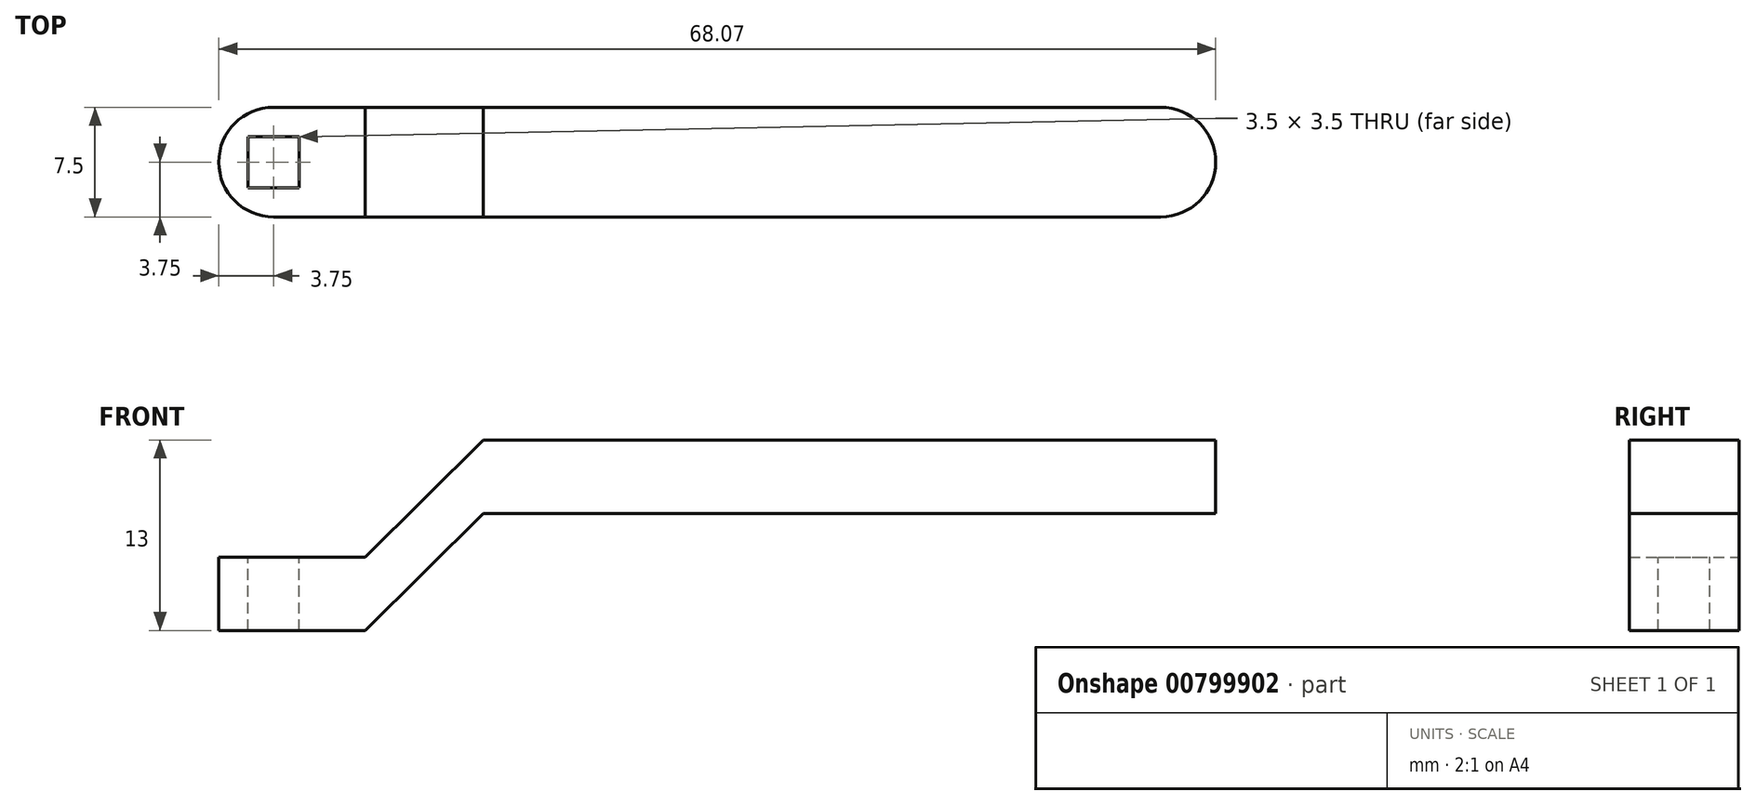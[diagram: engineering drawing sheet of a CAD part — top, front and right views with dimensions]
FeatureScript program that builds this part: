
annotation { "Feature Type Name" : "Feature", "Feature Type Description" : "" }
export const myFeature = defineFeature(function(context is Context, id is Id, definition is map)
    precondition{}
    {
        {
            var Q0;
            Q0=qCreatedBy(makeId("Front.planeOp"),FACE);
            var sketch = newSketch(context, id + "F0", { "sketchPlane" : qUnion([Q0])});
            skLineSegment(sketch, "E0", {"start": v(0, 0) * mm, "end": v(10, 0) * mm});
            skLineSegment(sketch, "E1", {"start": v(10, 0) * mm, "end": v(18.07, 8) * mm});
            skLineSegment(sketch, "E2", {"start": v(18.07, 8) * mm, "end": v(68.07, 8) * mm});
            skLineSegment(sketch, "E3", {"start": v(68.07, 8) * mm, "end": v(68.07, 13) * mm});
            skLineSegment(sketch, "E4", {"start": v(68.07, 13) * mm, "end": v(18.07, 13) * mm});
            skLineSegment(sketch, "E5", {"start": v(18.07, 13) * mm, "end": v(10, 5) * mm});
            skLineSegment(sketch, "E6", {"start": v(10, 5) * mm, "end": v(0, 5) * mm});
            skLineSegment(sketch, "E7", {"start": v(0, 5) * mm, "end": v(0, 0) * mm});
            skSolve(sketch);
        }
        {
            var Q0;
            Q0=makeQuery(id+"F0.imprint","IMPRINT",FACE,{"disambiguationData":[TD([[makeQuery(id+"F0.imprint","IMPRINT",EDGE,{"derivedFrom":sQuery(id+"F0.wireOp",EDGE,"E0")}),1.0]])]});
            extrude(context, id + "F1", {"entities" : qUnion([Q0]), "depth" : 3.75 * mm, "offsetDistance" : 25.4 * mm, "hasSecondDirection" : true, "secondDirectionOppositeDirection" : true, "secondDirectionDepth" : 3.75 * mm});
        }
        {
            var Q0;
            Q0=makeQuery(id+"F1.opExtrude","SWEPT_FACE",FACE,{"disambiguationData":[OSD([sQuery(id+"F0.wireOp",EDGE,"E6")])]});
            var sketch = newSketch(context, id + "F2", { "sketchPlane" : qUnion([Q0])});
            skPoint(sketch, "E8.centerSnap0", {"position": v(3.75, -3.75) * mm});
            skLineSegment(sketch, "E9.bottom", {"start": v(2, -1.75) * mm, "end": v(5.5, -1.75) * mm});
            skLineSegment(sketch, "E9.top", {"start": v(2, 1.75) * mm, "end": v(5.5, 1.75) * mm});
            skLineSegment(sketch, "E9.left", {"start": v(2, -1.75) * mm, "end": v(2, 1.75) * mm});
            skLineSegment(sketch, "E9.right", {"start": v(5.5, -1.75) * mm, "end": v(5.5, 1.75) * mm});
            skPoint(sketch, "E9.middle", {"position": v(3.75, 0) * mm});
            skSolve(sketch);
        }
        {
            var Q0;
            Q0=makeQuery(id+"F2.imprint","IMPRINT",FACE,{"disambiguationData":[TD([[makeQuery(id+"F2.imprint","IMPRINT",EDGE,{"derivedFrom":sQuery(id+"F2.wireOp",EDGE,"E9.bottom")}),1.0]])]});
            extrude(context, id + "F3", {"entities" : qUnion([Q0]), "operationType" : NewBodyOperationType.REMOVE, "endBound" : BoundingType.THROUGH_ALL, "oppositeDirection" : true, "depth" : 5 * mm, "offsetDistance" : 25.4 * mm});
        }
        {
            var Q0;
            Q0=makeQuery(id+"F1.opExtrude","CAP_EDGE",EDGE,{"disambiguationData":[OSD([sQuery(id+"F0.wireOp",EDGE,"E7")])],"isStart":false});
            var Q1;
            Q1=makeQuery(id+"F1.opExtrude","CAP_EDGE",EDGE,{"disambiguationData":[OSD([sQuery(id+"F0.wireOp",EDGE,"E7")])],"isStart":true});
            fillet(context, id + "F4", {"entities" : qUnion([Q0, Q1]), "radius" : 3.75 * mm, "tangentPropagation" : true, "allowEdgeOverflow" : false});
        }
        {
            var Q0;
            Q0=makeQuery(id+"F1.opExtrude","CAP_EDGE",EDGE,{"disambiguationData":[OSD([sQuery(id+"F0.wireOp",EDGE,"E3")])],"isStart":false});
            var Q1;
            Q1=makeQuery(id+"F1.opExtrude","CAP_EDGE",EDGE,{"disambiguationData":[OSD([sQuery(id+"F0.wireOp",EDGE,"E3")])],"isStart":true});
            fillet(context, id + "F5", {"entities" : qUnion([Q0, Q1]), "radius" : 3.75 * mm, "tangentPropagation" : true, "allowEdgeOverflow" : false});
        }
    });
